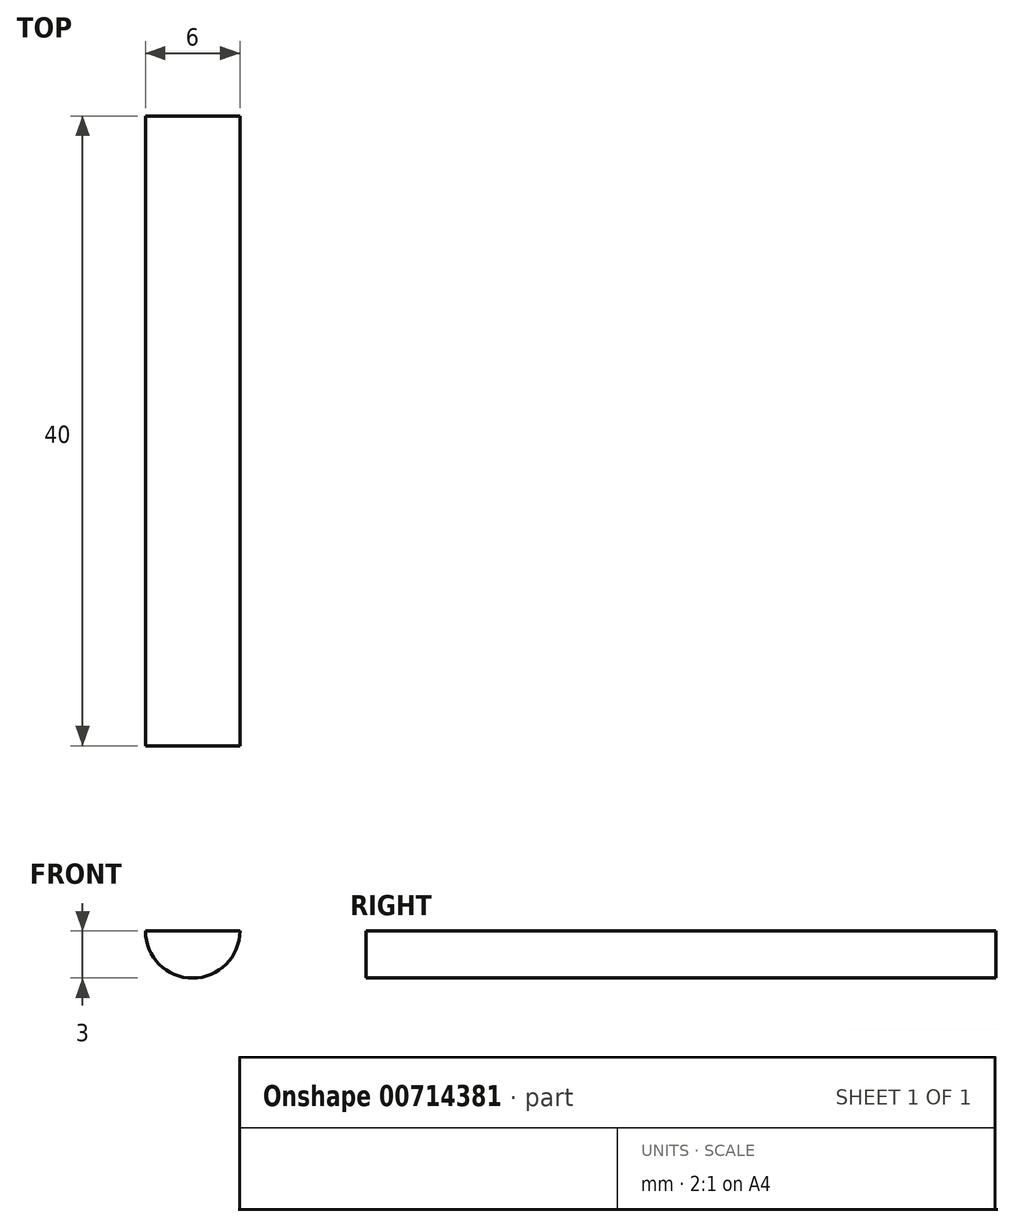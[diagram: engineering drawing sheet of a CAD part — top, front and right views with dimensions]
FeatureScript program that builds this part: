
annotation { "Feature Type Name" : "Feature", "Feature Type Description" : "" }
export const myFeature = defineFeature(function(context is Context, id is Id, definition is map)
    precondition{}
    {
        {
            var Q0;
            Q0=qCreatedBy(makeId("Front.planeOp"),FACE);
            var sketch = newSketch(context, id + "F0", { "sketchPlane" : qUnion([Q0])});
            skLineSegment(sketch, "E0", {"start": v(0, 0.64) * mm, "end": v(3, 0.64) * mm});
            skLineSegment(sketch, "E1", {"start": v(0, 0.64) * mm, "end": v(-3, 0.64) * mm});
            skArc(sketch, "E2", {"start": v(-3, 0.64) * mm, "mid": v(0, -2.36) * mm, "end": v(3, 0.64) * mm});
            skSolve(sketch);
        }
        {
            var Q0;
            Q0=makeQuery(id+"F0.imprint","IMPRINT",FACE,{"disambiguationData":[TD([[makeQuery(id+"F0.imprint","IMPRINT",EDGE,{"derivedFrom":sQuery(id+"F0.wireOp",EDGE,"E0")}),-1.0]])]});
            extrude(context, id + "F1", {"entities" : qUnion([Q0]), "depth" : 40 * mm, "offsetDistance" : 25 * mm});
        }
    });
